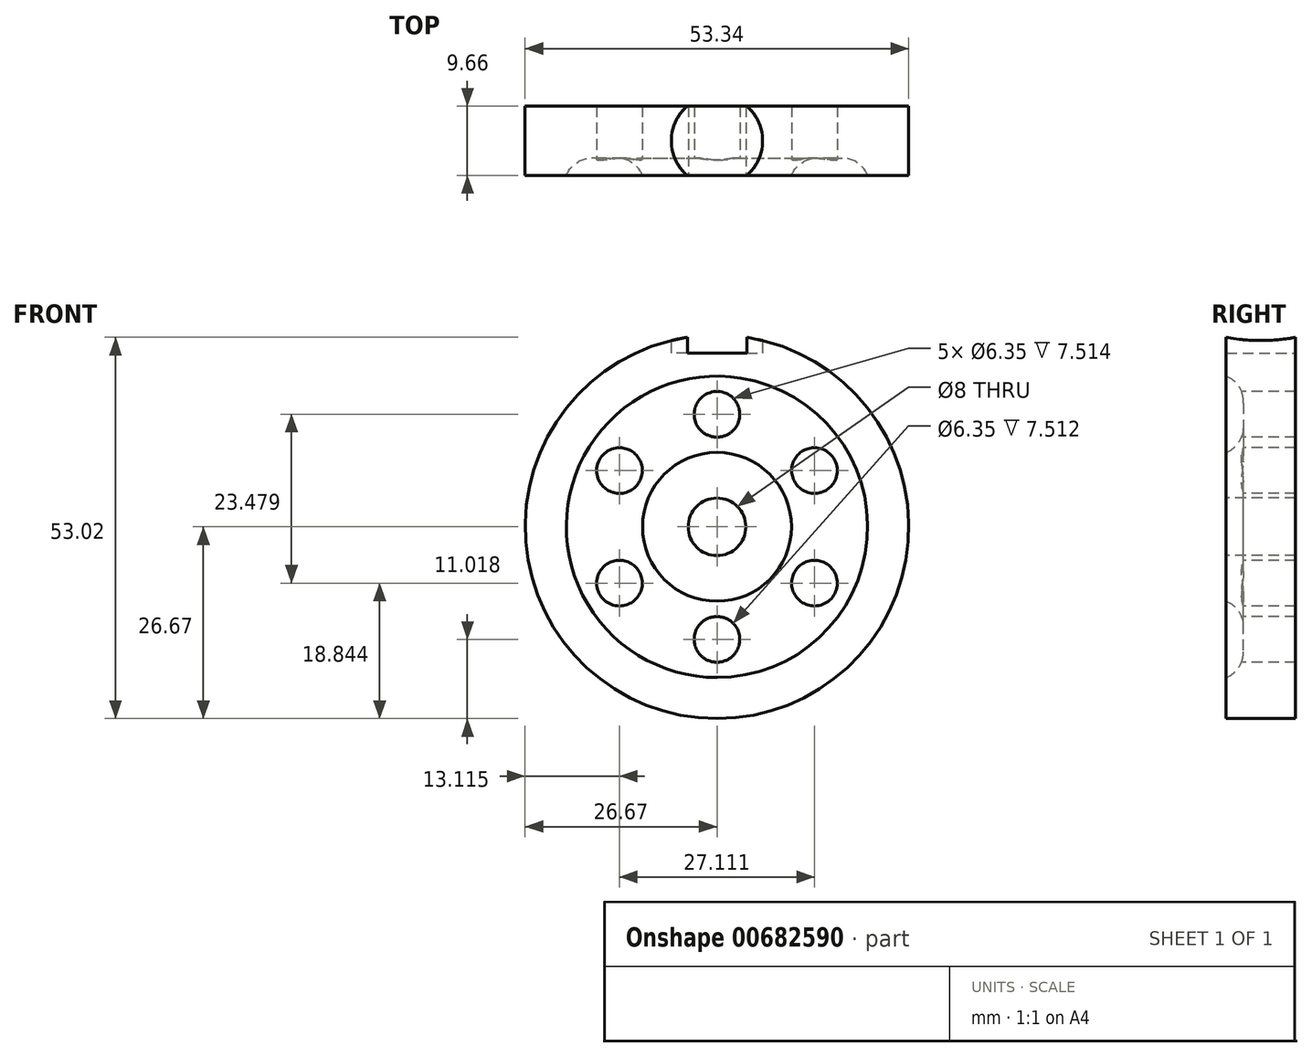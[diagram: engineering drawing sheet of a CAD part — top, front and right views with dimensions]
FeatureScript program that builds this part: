
annotation { "Feature Type Name" : "Feature", "Feature Type Description" : "" }
export const myFeature = defineFeature(function(context is Context, id is Id, definition is map)
    precondition{}
    {
        {
            var Q0;
            Q0=qCreatedBy(makeId("Front.planeOp"),FACE);
            var sketch = newSketch(context, id + "F0", { "sketchPlane" : qUnion([Q0])});
            skCircle(sketch, "E0", {"center": v(0, 0) * mm, "radius": 26.67 * mm});
            skSolve(sketch);
        }
        {
            var Q0;
            Q0 = qSketchRegion(id + "F0", true);
            extrude(context, id + "F1", {"entities" : qUnion([Q0]), "endBound" : BoundingType.SYMMETRIC, "depth" : 9.65 * mm, "offsetDistance" : 25.4 * mm});
        }
        {
            var Q0;
            Q0=qCreatedBy(makeId("Top.planeOp"),FACE);
            cPlane(context, id + "F2", {"entities" : qUnion([Q0]), "cplaneType" : CPlaneType.OFFSET, "offset" : 27.94 * mm, "width" : 152.4 * mm, "height" : 152.4 * mm});
        }
        {
            var Q0;
            Q0=qCreatedBy(id+"F2.planeOp",FACE);
            var sketch = newSketch(context, id + "F3", { "sketchPlane" : qUnion([Q0])});
            skCircle(sketch, "E1", {"center": v(0, 0) * mm, "radius": 6.35 * mm});
            skArc(sketch, "E2", {"start": v(2.77, 0.64) * mm, "mid": v(4.48, 1.85) * mm, "end": v(5.7, 3.56) * mm, "construction": true});
            skArc(sketch, "E3", {"start": v(-2.77, -0.64) * mm, "mid": v(-4.48, -1.85) * mm, "end": v(-5.7, -3.56) * mm, "construction": true});
            skLineSegment(sketch, "E4", {"start": v(0, 6.35) * mm, "end": v(0, 0) * mm, "construction": true});
            skLineSegment(sketch, "E5", {"start": v(0, 0) * mm, "end": v(0, -6.35) * mm, "construction": true});
            skLineSegment(sketch, "E6", {"start": v(-2.77, 0.63) * mm, "end": v(-2.77, -0.64) * mm, "construction": true});
            skLineSegment(sketch, "E7", {"start": v(2.77, 0.63) * mm, "end": v(2.77, -0.64) * mm, "construction": true});
            skLineSegment(sketch, "E8", {"start": v(-5.7, 3.56) * mm, "end": v(-5.7, 4.83) * mm, "construction": true});
            skLineSegment(sketch, "E9", {"start": v(5.7, 3.56) * mm, "end": v(5.7, 4.83) * mm, "construction": true});
            skLineSegment(sketch, "E10.MirrorCS", {"start": v(-5.7, -3.56) * mm, "end": v(-5.7, -4.83) * mm, "construction": true});
            skLineSegment(sketch, "E11.MirrorCS", {"start": v(5.7, -3.56) * mm, "end": v(5.7, -4.83) * mm, "construction": true});
            skArc(sketch, "E12.trimOffspring", {"start": v(-5.7, 3.56) * mm, "mid": v(-4.48, 1.85) * mm, "end": v(-2.77, 0.64) * mm, "construction": true});
            skArc(sketch, "E13.trimOffspring", {"start": v(5.7, -3.56) * mm, "mid": v(4.48, -1.85) * mm, "end": v(2.77, -0.64) * mm, "construction": true});
            skLineSegment(sketch, "E14", {"start": v(5.7, 4.83) * mm, "end": v(-5.7, 4.83) * mm, "construction": true});
            skLineSegment(sketch, "E15", {"start": v(-5.7, -4.83) * mm, "end": v(5.7, -4.83) * mm, "construction": true});
            skSolve(sketch);
        }
        {
            var Q0;
            Q0 = qSketchRegion(id + "F3", true);
            extrude(context, id + "F4", {"entities" : qUnion([Q0]), "operationType" : NewBodyOperationType.REMOVE, "oppositeDirection" : true, "depth" : 3.8 * mm, "offsetDistance" : 25.4 * mm});
        }
        {
            var Q0;
            Q0=makeQuery(id+"F1.opExtrude","CAP_FACE",FACE,{"disambiguationData":[OSD([sQuery(id+"F0.wireOp",EDGE,"E0")])],"isStart":false});
            var sketch = newSketch(context, id + "F5", { "sketchPlane" : qUnion([Q0])});
            skCircle(sketch, "E16", {"center": v(0, 0) * mm, "radius": 4 * mm});
            skSolve(sketch);
        }
        {
            var Q0;
            Q0 = qSketchRegion(id + "F5", true);
            extrude(context, id + "F6", {"entities" : qUnion([Q0]), "operationType" : NewBodyOperationType.REMOVE, "oppositeDirection" : true, "depth" : 41.4 * mm, "offsetDistance" : 25.4 * mm});
        }
        {
            var Q0;
            Q0=makeQuery(id+"F1.opExtrude","CAP_FACE",FACE,{"disambiguationData":[OSD([sQuery(id+"F0.wireOp",EDGE,"E0")])],"isStart":false});
            var sketch = newSketch(context, id + "F7", { "sketchPlane" : qUnion([Q0])});
            skCircle(sketch, "E17", {"center": v(0, 0) * mm, "radius": 10.35 * mm});
            skCircle(sketch, "E18", {"center": v(0, 0) * mm, "radius": 20.96 * mm});
            skSolve(sketch);
        }
        {
            var Q0;
            Q0 = qSketchRegion(id + "F7", true);
            extrude(context, id + "F8", {"entities" : qUnion([Q0]), "operationType" : NewBodyOperationType.REMOVE, "oppositeDirection" : true, "depth" : 2.41 * mm, "offsetDistance" : 25.4 * mm});
        }
        {
            var Q0;
            Q0=makeQuery(id+"F8.boolean.opBoolean","COPY",FACE,{"derivedFrom":makeQuery(id+"F8.opExtrude","CAP_FACE",FACE,{"disambiguationData":[OSD([sQuery(id+"F7.wireOp",EDGE,"E17"),sQuery(id+"F7.wireOp",EDGE,"E18")])],"isStart":false})});
            var sketch = newSketch(context, id + "F9", { "sketchPlane" : qUnion([Q0])});
            skCircle(sketch, "E19", {"center": v(0, 15.65) * mm, "radius": 3.18 * mm});
            skLineSegment(sketch, "E20", {"start": v(0, 15.65) * mm, "end": v(0, 20.96) * mm});
            skLineSegment(sketch, "E21", {"start": v(0, 15.65) * mm, "end": v(0, 10.35) * mm});
            skCircle(sketch, "E22.1.0", {"center": v(-13.56, 7.83) * mm, "radius": 3.18 * mm});
            skCircle(sketch, "E22.2.0", {"center": v(-13.56, -7.83) * mm, "radius": 3.18 * mm});
            skCircle(sketch, "E22.3.0", {"center": v(0, -15.65) * mm, "radius": 3.18 * mm});
            skCircle(sketch, "E22.4.0", {"center": v(13.56, -7.83) * mm, "radius": 3.18 * mm});
            skCircle(sketch, "E22.5.0", {"center": v(13.56, 7.83) * mm, "radius": 3.18 * mm});
            skPoint(sketch, "E22.center", {"position": v(0, 0) * mm});
            skSolve(sketch);
        }
        {
            var Q0;
            Q0 = qSketchRegion(id + "F9", true);
            var Q1;
            Q1 = qConstructionFilter(qBodyType(qCreatedBy(id + "F9" ,EDGE), BodyType.WIRE), ConstructionObject.NO);
            extrude(context, id + "F10", {"entities" : qUnion([Q0]), "operationType" : NewBodyOperationType.REMOVE, "surfaceEntities" : qUnion([Q1]), "oppositeDirection" : true, "depth" : 25.4 * mm, "offsetDistance" : 25.4 * mm});
        }
        {
            var Q0;
            Q0=makeQuery(id+"F8.boolean.opBoolean","COPY",EDGE,{"derivedFrom":makeQuery(id+"F8.opExtrude","CAP_EDGE",EDGE,{"disambiguationData":[OSD([sQuery(id+"F7.wireOp",EDGE,"E18")])],"isStart":false})});
            var Q1;
            Q1=makeQuery(id+"F8.boolean.opBoolean","COPY",EDGE,{"derivedFrom":makeQuery(id+"F8.opExtrude","CAP_EDGE",EDGE,{"disambiguationData":[OSD([sQuery(id+"F7.wireOp",EDGE,"E17")])],"isStart":false})});
            var Q2;
            Q2=makeQuery(id+"FceMFZ39dj65BmD_1.1.F8.boolean.opBoolean","COPY",EDGE,{"derivedFrom":makeQuery(id+"FceMFZ39dj65BmD_1.1.F8.opExtrude","CAP_EDGE",EDGE,{"disambiguationData":[OSD([sQuery(id+"F7.wireOp",EDGE,"E18")])],"isStart":false})});
            var Q3;
            Q3=makeQuery(id+"FceMFZ39dj65BmD_1.1.F8.boolean.opBoolean","COPY",EDGE,{"derivedFrom":makeQuery(id+"FceMFZ39dj65BmD_1.1.F8.opExtrude","CAP_EDGE",EDGE,{"disambiguationData":[OSD([sQuery(id+"F7.wireOp",EDGE,"E17")])],"isStart":false})});
            fillet(context, id + "F11", {"entities" : qUnion([Q0, Q1, Q2, Q3]), "radius" : 3.8 * mm, "tangentPropagation" : true, "allowEdgeOverflow" : false});
        }
    });
